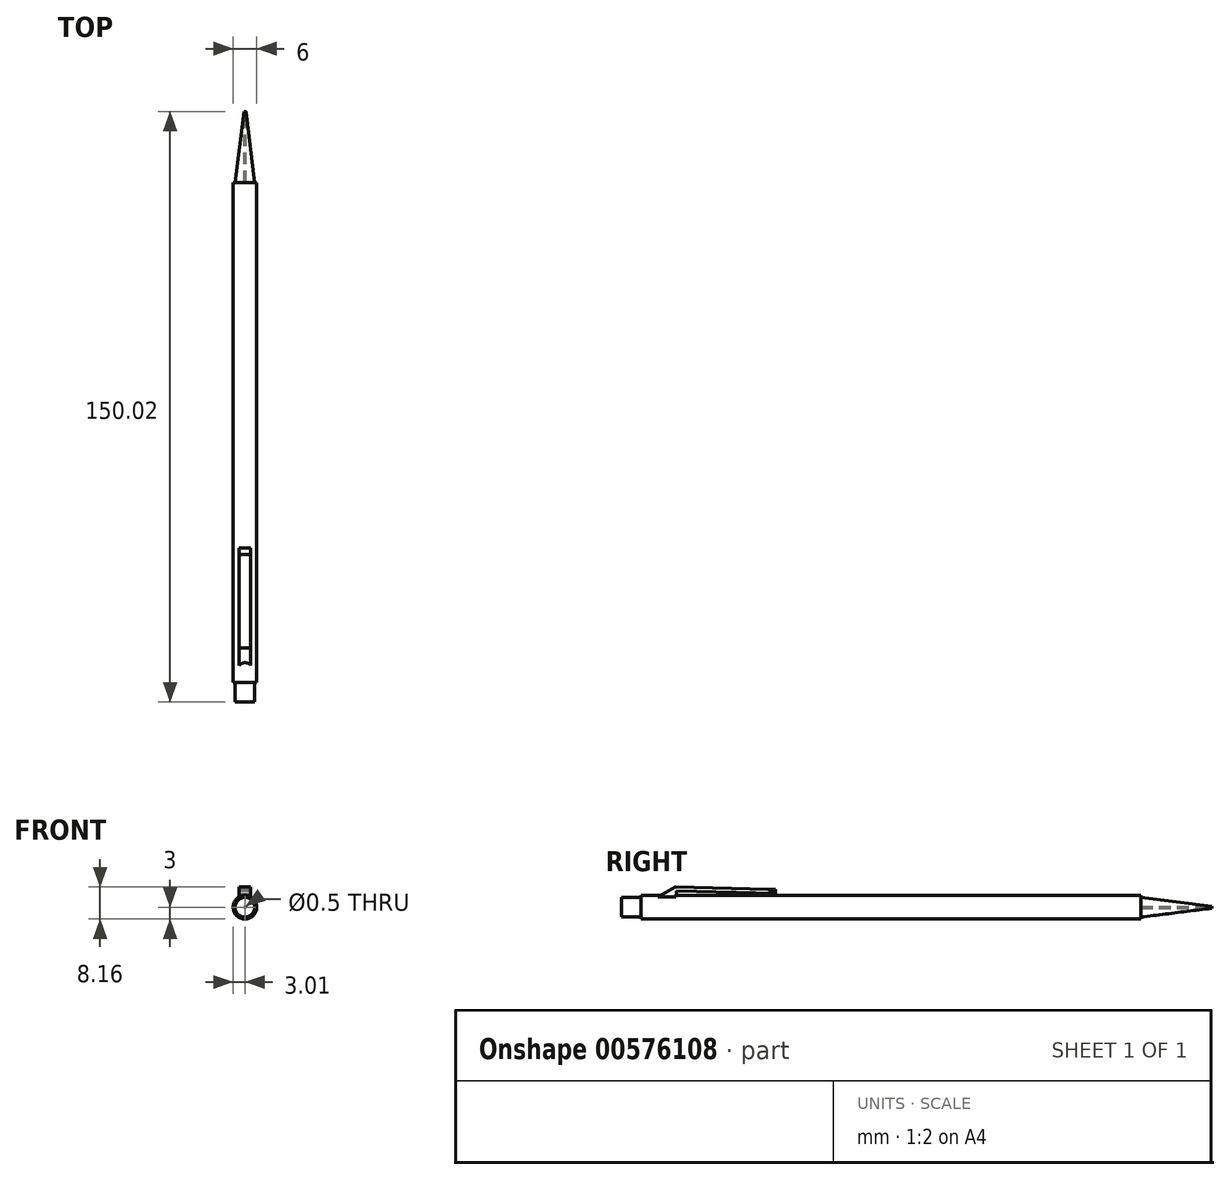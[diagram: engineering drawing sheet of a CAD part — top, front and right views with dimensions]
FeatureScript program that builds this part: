
annotation { "Feature Type Name" : "Feature", "Feature Type Description" : "" }
export const myFeature = defineFeature(function(context is Context, id is Id, definition is map)
    precondition{}
    {
        {
            var Q0;
            Q0=qCreatedBy(makeId("Front.planeOp"),FACE);
            var sketch = newSketch(context, id + "F0", { "sketchPlane" : qUnion([Q0])});
            skCircle(sketch, "E0", {"center": v(0, 0) * mm, "radius": 3 * mm});
            skSolve(sketch);
        }
        {
            var Q0;
            Q0=makeQuery(id+"F0.imprint","IMPRINT",FACE,{"disambiguationData":[TD([[makeQuery(id+"F0.imprint","IMPRINT",EDGE,{"derivedFrom":sQuery(id+"F0.wireOp",EDGE,"E0")}),1.0]])]});
            extrude(context, id + "F1", {"entities" : qUnion([Q0]), "oppositeDirection" : true, "depth" : 127 * mm, "offsetDistance" : 25 * mm});
        }
        {
            var Q0;
            Q0=makeQuery(id+"F1.opExtrude","CAP_FACE",FACE,{"disambiguationData":[OSD([sQuery(id+"F0.wireOp",EDGE,"E0")])],"isStart":true});
            var sketch = newSketch(context, id + "F2", { "sketchPlane" : qUnion([Q0])});
            skCircle(sketch, "E1", {"center": v(0, 0) * mm, "radius": 2.5 * mm});
            skSolve(sketch);
        }
        {
            var Q0;
            Q0=qCreatedBy(makeId("Top.planeOp"),FACE);
            var sketch = newSketch(context, id + "F3", { "sketchPlane" : qUnion([Q0])});
            skLineSegment(sketch, "E2", {"start": v(0.01, 127.02) * mm, "end": v(-2.49, 127.02) * mm});
            skLineSegment(sketch, "E3", {"start": v(0.01, 127.02) * mm, "end": v(0.01, 145.02) * mm});
            skLineSegment(sketch, "E4", {"start": v(0.01, 145.02) * mm, "end": v(-0.24, 145.02) * mm});
            skLineSegment(sketch, "E5", {"start": v(-0.24, 145.02) * mm, "end": v(-2.49, 127.02) * mm});
            skSolve(sketch);
        }
        {
            var Q0;
            Q0=makeQuery(id+"F3.imprint","IMPRINT",FACE,{"disambiguationData":[TD([[makeQuery(id+"F3.imprint","IMPRINT",EDGE,{"derivedFrom":sQuery(id+"F3.wireOp",EDGE,"E2")}),-1.0]])]});
            var Q1;
            Q1=sQuery(id+"F3.wireOp",EDGE,"E3");
            revolve(context, id + "F4", {"entities" : qUnion([Q0]), "axis" : qUnion([Q1]), "revolveType" : RevolveType.FULL});
        }
        {
            var Q0;
            Q0=makeQuery(id+"F4.opRevolve","SWEPT_FACE",FACE,{"disambiguationData":[OSD([sQuery(id+"F3.wireOp",EDGE,"E4")])]});
            extrude(context, id + "F5", {"entities" : qUnion([Q0]), "operationType" : NewBodyOperationType.REMOVE, "oppositeDirection" : true, "depth" : 18 * mm, "offsetDistance" : 25 * mm});
        }
        {
            var Q0;
            Q0=qCreatedBy(makeId("Right.planeOp"),FACE);
            var sketch = newSketch(context, id + "F6", { "sketchPlane" : qUnion([Q0])});
            skLineSegment(sketch, "E6", {"start": v(0.9, 2.55) * mm, "end": v(6, 2.55) * mm});
            skLineSegment(sketch, "E7", {"start": v(6, 2.55) * mm, "end": v(8.96, 4.26) * mm});
            skLineSegment(sketch, "E8", {"start": v(8.96, 4.26) * mm, "end": v(33.95, 3.65) * mm});
            skSolve(sketch);
        }
        {
            var Q0;
            Q0=qCreatedBy(makeId("Top.planeOp"),FACE);
            cPlane(context, id + "F7", {"entities" : qUnion([Q0]), "cplaneType" : CPlaneType.OFFSET, "offset" : 3 * mm, "width" : 150 * mm, "height" : 150 * mm});
        }
        {
            var Q0;
            Q0=qCreatedBy(id+"F7.planeOp",FACE);
            var sketch = newSketch(context, id + "F8", { "sketchPlane" : qUnion([Q0])});
            skPoint(sketch, "E9.0", {"position": v(0, 6) * mm});
            skLineSegment(sketch, "E10", {"start": v(0, 6) * mm, "end": v(0, 7) * mm});
            skLineSegment(sketch, "E11", {"start": v(0, 7) * mm, "end": v(1.5, 7) * mm});
            skLineSegment(sketch, "E12", {"start": v(1.5, 7) * mm, "end": v(1.5, 5) * mm});
            skLineSegment(sketch, "E13", {"start": v(1.5, 5) * mm, "end": v(-1.5, 5) * mm});
            skLineSegment(sketch, "E14", {"start": v(-1.5, 5) * mm, "end": v(-1.5, 7) * mm});
            skLineSegment(sketch, "E15", {"start": v(-1.5, 7) * mm, "end": v(0, 7) * mm});
            skSolve(sketch);
        }
        {
            var Q0;
            Q0=makeQuery(id+"F2.imprint","IMPRINT",FACE,{"disambiguationData":[TD([[makeQuery(id+"F2.imprint","IMPRINT",EDGE,{"derivedFrom":sQuery(id+"F2.wireOp",EDGE,"E1")}),1.0]])]});
            extrude(context, id + "F9", {"entities" : qUnion([Q0]), "depth" : 5 * mm, "offsetDistance" : 25 * mm});
        }
        {
            var Q0;
            Q0=makeQuery(id+"F8.imprint","IMPRINT",FACE,{"disambiguationData":[TD([[makeQuery(id+"F8.imprint","IMPRINT",EDGE,{"derivedFrom":sQuery(id+"F8.wireOp",EDGE,"E11")}),-1.0]])]});
            var Q1;
            Q1=sQuery(id+"F8.wireOp",EDGE,"E15");
            var Q2;
            Q2=sQuery(id+"F6.wireOp",EDGE,"E7");
            var Q3;
            Q3=sQuery(id+"F6.wireOp",EDGE,"E8");
            sweep(context, id + "F10", {"operationType" : NewBodyOperationType.ADD, "profiles" : qUnion([Q0]), "surfaceProfiles" : qUnion([Q1]), "path" : qUnion([Q2, Q3])});
        }
        {
            var Q0;
            Q0=makeQuery(id+"F10.opSweep","SWEPT_FACE",FACE,{"disambiguationData":[OSD([sQuery(id+"F6.wireOp",EDGE,"E7"),sQuery(id+"F8.wireOp",EDGE,"E14")])]});
            var sketch = newSketch(context, id + "F11", { "sketchPlane" : qUnion([Q0])});
            skLineSegment(sketch, "E16", {"start": v(-8.99, 4.15) * mm, "end": v(-8.95, 2.6) * mm});
            skLineSegment(sketch, "E17", {"start": v(-8.95, 2.6) * mm, "end": v(-6.3, 2.6) * mm});
            skLineSegment(sketch, "E18", {"start": v(-6.3, 2.6) * mm, "end": v(-8.99, 4.15) * mm});
            skSolve(sketch);
        }
        {
            var Q0;
            Q0=makeQuery(id+"F11.imprint","IMPRINT",FACE,{"disambiguationData":[TD([[makeQuery(id+"F11.imprint","IMPRINT",EDGE,{"derivedFrom":sQuery(id+"F11.wireOp",EDGE,"E16")}),1.0]])]});
            extrude(context, id + "F12", {"entities" : qUnion([Q0]), "operationType" : NewBodyOperationType.ADD, "oppositeDirection" : true, "depth" : 3 * mm, "offsetDistance" : 25 * mm});
        }
        {
            var Q0;
            Q0=makeQuery(id+"F12.boolean.opBoolean","MERGE",FACE,{"derivedFrom":[makeQuery(id+"F10.opSweep","SWEPT_FACE",FACE,{"disambiguationData":[OSD([sQuery(id+"F6.wireOp",EDGE,"E7"),sQuery(id+"F8.wireOp",EDGE,"E12")])]}),makeQuery(id+"F12.opExtrude","CAP_FACE",FACE,{"disambiguationData":[OSD([sQuery(id+"F11.wireOp",EDGE,"E16"),sQuery(id+"F11.wireOp",EDGE,"E17"),sQuery(id+"F11.wireOp",EDGE,"E18")])],"isStart":false})]});
            var sketch = newSketch(context, id + "F13", { "sketchPlane" : qUnion([Q0])});
            skLineSegment(sketch, "E19", {"start": v(32.44, 4.58) * mm, "end": v(34.14, 4.58) * mm});
            skLineSegment(sketch, "E20", {"start": v(34.14, 4.58) * mm, "end": v(34.14, 3.54) * mm});
            skLineSegment(sketch, "E21", {"start": v(34.14, 3.54) * mm, "end": v(32.44, 4.58) * mm});
            skSolve(sketch);
        }
        {
            var Q0;
            Q0=makeQuery(id+"F13.imprint","IMPRINT",FACE,{"disambiguationData":[TD([[makeQuery(id+"F13.imprint","IMPRINT",EDGE,{"derivedFrom":sQuery(id+"F13.wireOp",EDGE,"E19")}),-1.0]])]});
            extrude(context, id + "F14", {"entities" : qUnion([Q0]), "oppositeDirection" : true, "depth" : 3 * mm, "offsetDistance" : 25 * mm});
        }
    });
